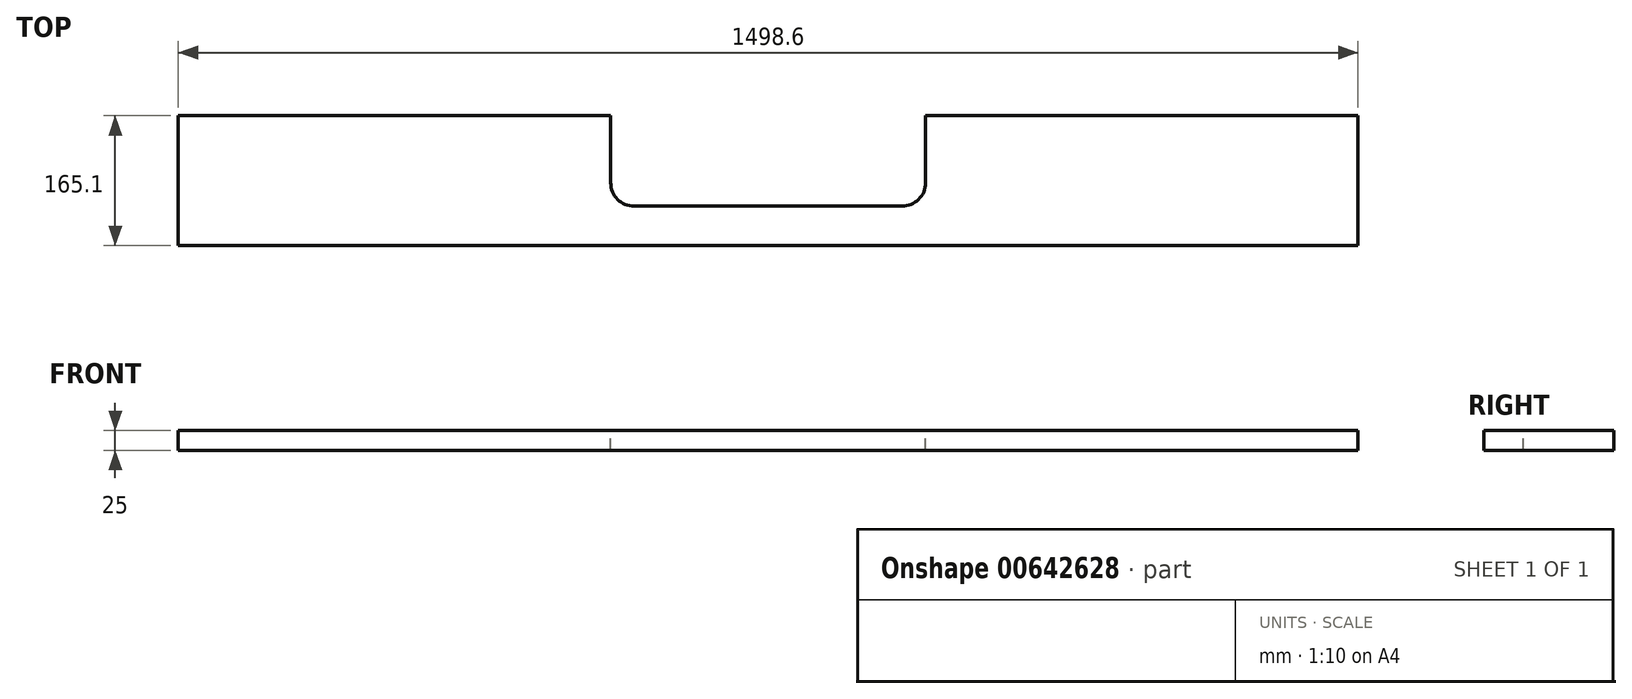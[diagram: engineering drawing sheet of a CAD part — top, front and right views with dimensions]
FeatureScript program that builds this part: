
annotation { "Feature Type Name" : "Feature", "Feature Type Description" : "" }
export const myFeature = defineFeature(function(context is Context, id is Id, definition is map)
    precondition{}
    {
        {
            var Q0;
            Q0=qCreatedBy(makeId("Top.planeOp"),FACE);
            var sketch = newSketch(context, id + "F0", { "sketchPlane" : qUnion([Q0])});
            skLineSegment(sketch, "E0.bottom", {"start": v(-749.3, 82.55) * mm, "end": v(749.3, 82.55) * mm});
            skLineSegment(sketch, "E0.top", {"start": v(-749.3, -82.55) * mm, "end": v(749.3, -82.55) * mm});
            skLineSegment(sketch, "E0.left", {"start": v(-749.3, 82.55) * mm, "end": v(-749.3, -82.55) * mm});
            skLineSegment(sketch, "E0.right", {"start": v(749.3, 82.55) * mm, "end": v(749.3, -82.55) * mm});
            skPoint(sketch, "E0.middle", {"position": v(0, 0) * mm});
            skSolve(sketch);
        }
        {
            var Q0;
            Q0=makeQuery(id+"F0.imprint","IMPRINT",FACE,{"disambiguationData":[TD([[makeQuery(id+"F0.imprint","IMPRINT",EDGE,{"derivedFrom":sQuery(id+"F0.wireOp",EDGE,"E0.bottom")}),-1.0]])]});
            extrude(context, id + "F1", {"entities" : qUnion([Q0]), "depth" : 25 * mm, "offsetDistance" : 25 * mm});
        }
        {
            var Q0;
            Q0=makeQuery(id+"F1.opExtrude","CAP_FACE",FACE,{"disambiguationData":[OSD([sQuery(id+"F0.wireOp",EDGE,"E0.bottom"),sQuery(id+"F0.wireOp",EDGE,"E0.top"),sQuery(id+"F0.wireOp",EDGE,"E0.left"),sQuery(id+"F0.wireOp",EDGE,"E0.right")])],"isStart":false});
            var sketch = newSketch(context, id + "F2", { "sketchPlane" : qUnion([Q0])});
            skLineSegment(sketch, "E1", {"start": v(-200, 82.55) * mm, "end": v(-200, -2.55) * mm});
            skLineSegment(sketch, "E2", {"start": v(-170, -32.55) * mm, "end": v(0, -32.55) * mm});
            skPoint(sketch, "E3.visualSharp", {"position": v(-200, -32.55) * mm});
            skArc(sketch, "E3.filletArc", {"start": v(-200, -2.55) * mm, "mid": v(-191.21, -23.76) * mm, "end": v(-170, -32.55) * mm});
            skLineSegment(sketch, "E4.MirrorCS", {"start": v(200, 82.55) * mm, "end": v(200, -2.55) * mm});
            skArc(sketch, "E5.MirrorCS", {"start": v(200, -2.55) * mm, "mid": v(191.21, -23.76) * mm, "end": v(170, -32.55) * mm});
            skLineSegment(sketch, "E6.MirrorCS", {"start": v(170, -32.55) * mm, "end": v(0, -32.55) * mm});
            skLineSegment(sketch, "E7", {"start": v(-200, 82.55) * mm, "end": v(200, 82.55) * mm});
            skSolve(sketch);
        }
        {
            var Q0;
            Q0=makeQuery(id+"F2.imprint","IMPRINT",FACE,{"disambiguationData":[TD([[makeQuery(id+"F2.imprint","IMPRINT",EDGE,{"derivedFrom":sQuery(id+"F2.wireOp",EDGE,"E1")}),1.0]])]});
            extrude(context, id + "F3", {"entities" : qUnion([Q0]), "operationType" : NewBodyOperationType.REMOVE, "endBound" : BoundingType.UP_TO_NEXT, "oppositeDirection" : true, "depth" : 25 * mm, "offsetDistance" : 25 * mm});
        }
        {
            var Q0;
            Q0=makeQuery(id+"F1.opExtrude","SWEPT_BODY",BODY,{"disambiguationData":[OSD([sQuery(id+"F0.wireOp",EDGE,"E0.bottom"),sQuery(id+"F0.wireOp",EDGE,"E0.top"),sQuery(id+"F0.wireOp",EDGE,"E0.left"),sQuery(id+"F0.wireOp",EDGE,"E0.right")])]});
            transform(context, id + "F4", {"entities" : qUnion([Q0]), "transformType" : TransformType.TRANSLATION_3D, "dx" : 0 * mm, "dy" : 0 * mm, "dz" : 0 * mm, "makeCopy" : true});
        }
    });
